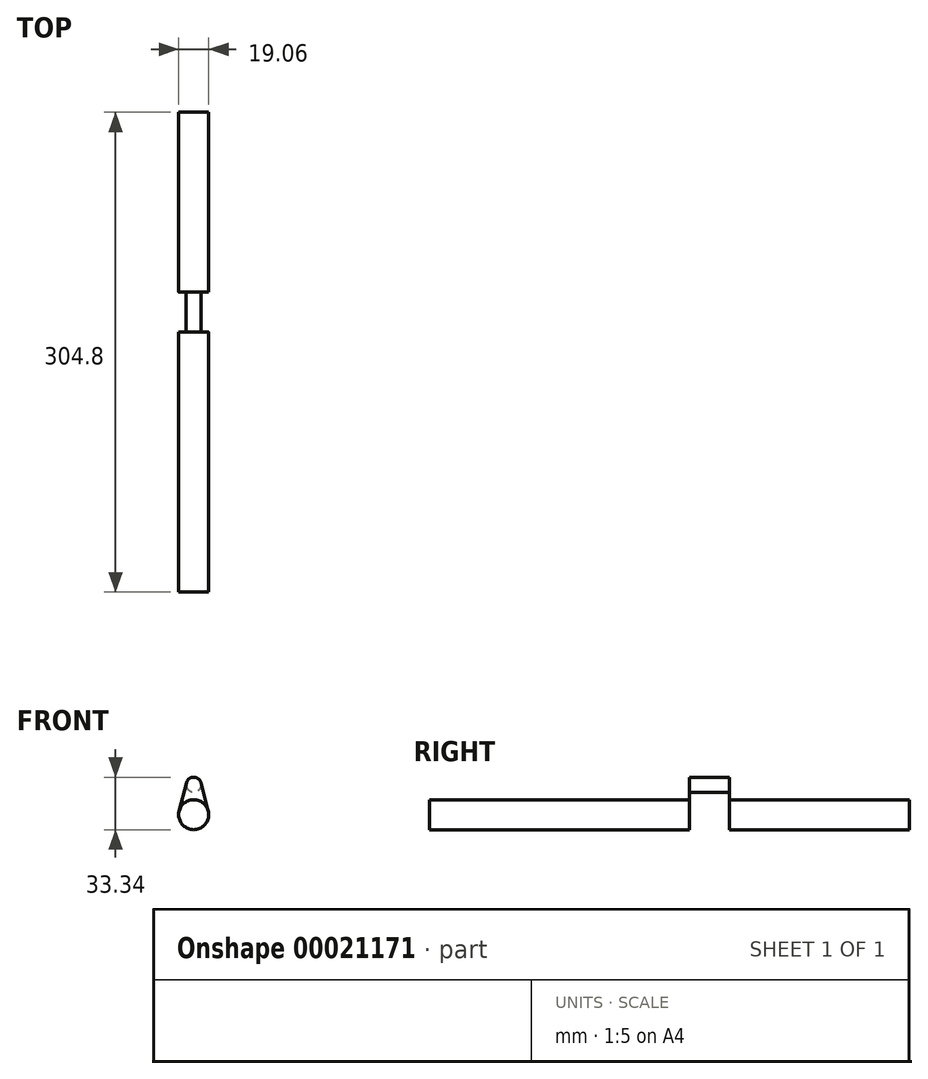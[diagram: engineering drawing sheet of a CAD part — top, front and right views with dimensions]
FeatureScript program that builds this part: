
annotation { "Feature Type Name" : "Feature", "Feature Type Description" : "" }
export const myFeature = defineFeature(function(context is Context, id is Id, definition is map)
    precondition{}
    {
        {
            var Q0;
            Q0=qCreatedBy(makeId("Front.planeOp"),FACE);
            var sketch = newSketch(context, id + "F0", { "sketchPlane" : qUnion([Q0])});
            skCircle(sketch, "E0", {"center": v(0, 0) * mm, "radius": 9.53 * mm});
            skSolve(sketch);
        }
        {
            var Q0;
            Q0 = qSketchRegion(id + "F0", true);
            extrude(context, id + "F1", {"entities" : qUnion([Q0]), "depth" : 114.3 * mm});
        }
        {
            var Q0;
            Q0=makeQuery(id+"F1.opExtrude","CAP_FACE",FACE,{"disambiguationData":[OSD([sQuery(id+"F0.wireOp",EDGE,"E0")])],"isStart":false});
            var sketch = newSketch(context, id + "F2", { "sketchPlane" : qUnion([Q0])});
            skLineSegment(sketch, "E1", {"start": v(-4.61, 20.24) * mm, "end": v(-9.22, 2.38) * mm});
            skLineSegment(sketch, "E2", {"start": v(0, -9.53) * mm, "end": v(0, -9.53) * mm});
            skLineSegment(sketch, "E3", {"start": v(9.22, 2.38) * mm, "end": v(4.61, 20.24) * mm});
            skLineSegment(sketch, "E4", {"start": v(0, 23.81) * mm, "end": v(0, 23.81) * mm});
            skCircle(sketch, "E5", {"center": v(0, 19.05) * mm, "radius": 4.76 * mm});
            skPoint(sketch, "E6.visualSharp", {"position": v(-12.3, -9.53) * mm});
            skArc(sketch, "E6.filletArc", {"start": v(-9.22, 2.38) * mm, "mid": v(-7.53, -5.83) * mm, "end": v(0, -9.53) * mm});
            skPoint(sketch, "E7.visualSharp", {"position": v(12.3, -9.53) * mm});
            skArc(sketch, "E7.filletArc", {"start": v(0, -9.53) * mm, "mid": v(7.53, -5.83) * mm, "end": v(9.22, 2.38) * mm});
            skPoint(sketch, "E8.visualSharp", {"position": v(-3.69, 23.81) * mm});
            skArc(sketch, "E8.filletArc", {"start": v(0, 23.81) * mm, "mid": v(-2.92, 22.82) * mm, "end": v(-4.61, 20.24) * mm});
            skPoint(sketch, "E9.visualSharp", {"position": v(3.69, 23.81) * mm});
            skArc(sketch, "E9.filletArc", {"start": v(4.61, 20.24) * mm, "mid": v(2.92, 22.82) * mm, "end": v(0, 23.81) * mm});
            skSolve(sketch);
        }
        {
            var Q0;
            {var subQ2=sQuery(id+"F2.wireOp",EDGE,"E6.filletArc");Q0=makeQuery(id+"F2.imprint","IMPRINT",FACE,{"disambiguationData":[TD([[makeQuery(id+"F2.imprint","IMPRINT",EDGE,{"derivedFrom":subQ2}),1.0]])]});}
            var Q1;
            {var subQ2=sQuery(id+"F2.wireOp",EDGE,"E1");Q1=makeQuery(id+"F2.imprint","IMPRINT",FACE,{"disambiguationData":[TD([[makeQuery(id+"F2.imprint","IMPRINT",EDGE,{"derivedFrom":subQ2}),1.0]])]});}
            var Q2;
            {var subQ0=sQuery(id+"F2.wireOp",EDGE,"E5");var subQ2=makeQuery(id+"F2.imprint","INTERSECT",VERTEX,{"derivedFrom":[sQuery(id+"F2.wireOp",EDGE,"E1"),subQ0]});Q2=makeQuery(id+"F2.imprint","IMPRINT",FACE,{"disambiguationData":[TD([[makeQuery(id+"F2.imprint","IMPRINT",EDGE,{"disambiguationData":[TD([[subQ2,1.0]])],"derivedFrom":subQ0}),1.0]])]});}
            extrude(context, id + "F3", {"entities" : qUnion([Q0, Q1, Q2]), "operationType" : NewBodyOperationType.ADD, "depth" : 1 / 203.2 * mm});
        }
        {
            var Q0;
            {var subQ0=sQuery(id+"F2.wireOp",EDGE,"E5");var subQ2=makeQuery(id+"F2.imprint","INTERSECT",VERTEX,{"derivedFrom":[sQuery(id+"F2.wireOp",EDGE,"E1"),subQ0]});Q0=makeQuery(id+"F2.imprint","IMPRINT",FACE,{"disambiguationData":[TD([[makeQuery(id+"F2.imprint","IMPRINT",EDGE,{"disambiguationData":[TD([[subQ2,1.0]])],"derivedFrom":subQ0}),1.0]])]});}
            extrude(context, id + "F4", {"entities" : qUnion([Q0]), "operationType" : NewBodyOperationType.ADD, "depth" : 25.4 * mm});
        }
        {
            var Q0;
            Q0=makeQuery(id+"F4.opExtrude","CAP_FACE",FACE,{"disambiguationData":[OSD([sQuery(id+"F2.wireOp",EDGE,"E5")])],"isStart":false});
            var sketch = newSketch(context, id + "F5", { "sketchPlane" : qUnion([Q0])});
            skCircle(sketch, "E10.0", {"center": v(0, 19.05) * mm, "radius": 4.76 * mm});
            skLineSegment(sketch, "E11.0", {"start": v(-4.61, 20.24) * mm, "end": v(-9.22, 2.38) * mm});
            skCircle(sketch, "E12.0", {"center": v(0, 0) * mm, "radius": 9.53 * mm});
            skLineSegment(sketch, "E13.0", {"start": v(9.22, 2.38) * mm, "end": v(4.61, 20.24) * mm});
            skSolve(sketch);
        }
        {
            var Q0;
            {var subQ0=sQuery(id+"F5.wireOp",EDGE,"E10.0");var subQ2=makeQuery(id+"F5.imprint","INTERSECT",VERTEX,{"derivedFrom":[subQ0,sQuery(id+"F5.wireOp",EDGE,"E11.0")]});Q0=makeQuery(id+"F5.imprint","IMPRINT",FACE,{"disambiguationData":[TD([[makeQuery(id+"F5.imprint","IMPRINT",EDGE,{"disambiguationData":[TD([[subQ2,1.0]])],"derivedFrom":subQ0}),1.0]])]});}
            var Q1;
            {var subQ2=sQuery(id+"F5.wireOp",EDGE,"E11.0");Q1=makeQuery(id+"F5.imprint","IMPRINT",FACE,{"disambiguationData":[TD([[makeQuery(id+"F5.imprint","IMPRINT",EDGE,{"derivedFrom":subQ2}),1.0]])]});}
            var Q2;
            {var subQ0=sQuery(id+"F5.wireOp",EDGE,"E12.0");var subQ2=makeQuery(id+"F5.imprint","INTERSECT",VERTEX,{"derivedFrom":[sQuery(id+"F5.wireOp",EDGE,"E11.0"),subQ0]});Q2=makeQuery(id+"F5.imprint","IMPRINT",FACE,{"disambiguationData":[TD([[makeQuery(id+"F5.imprint","IMPRINT",EDGE,{"disambiguationData":[TD([[subQ2,1.0]])],"derivedFrom":subQ0}),1.0]])]});}
            extrude(context, id + "F6", {"entities" : qUnion([Q0, Q1, Q2]), "operationType" : NewBodyOperationType.ADD, "oppositeDirection" : true, "depth" : 1 / 203.2 * mm});
        }
        {
            var Q0;
            Q0=makeQuery(id+"F6.boolean.opBoolean","MERGE",FACE,{"derivedFrom":[makeQuery(id+"F4.opExtrude","CAP_FACE",FACE,{"disambiguationData":[OSD([sQuery(id+"F2.wireOp",EDGE,"E5")])],"isStart":false}),makeQuery(id+"F6.opExtrude","CAP_FACE",FACE,{"disambiguationData":[OSD([sQuery(id+"F5.wireOp",EDGE,"E10.0"),sQuery(id+"F5.wireOp",EDGE,"E11.0"),sQuery(id+"F5.wireOp",EDGE,"E12.0"),sQuery(id+"F5.wireOp",EDGE,"E13.0")])],"isStart":true})]});
            var sketch = newSketch(context, id + "F7", { "sketchPlane" : qUnion([Q0])});
            skCircle(sketch, "E14.0", {"center": v(0, 0) * mm, "radius": 9.53 * mm});
            skSolve(sketch);
        }
        {
            var Q0;
            Q0 = qSketchRegion(id + "F7", true);
            extrude(context, id + "F8", {"entities" : qUnion([Q0]), "operationType" : NewBodyOperationType.ADD, "depth" : 165.1 * mm});
        }
    });
